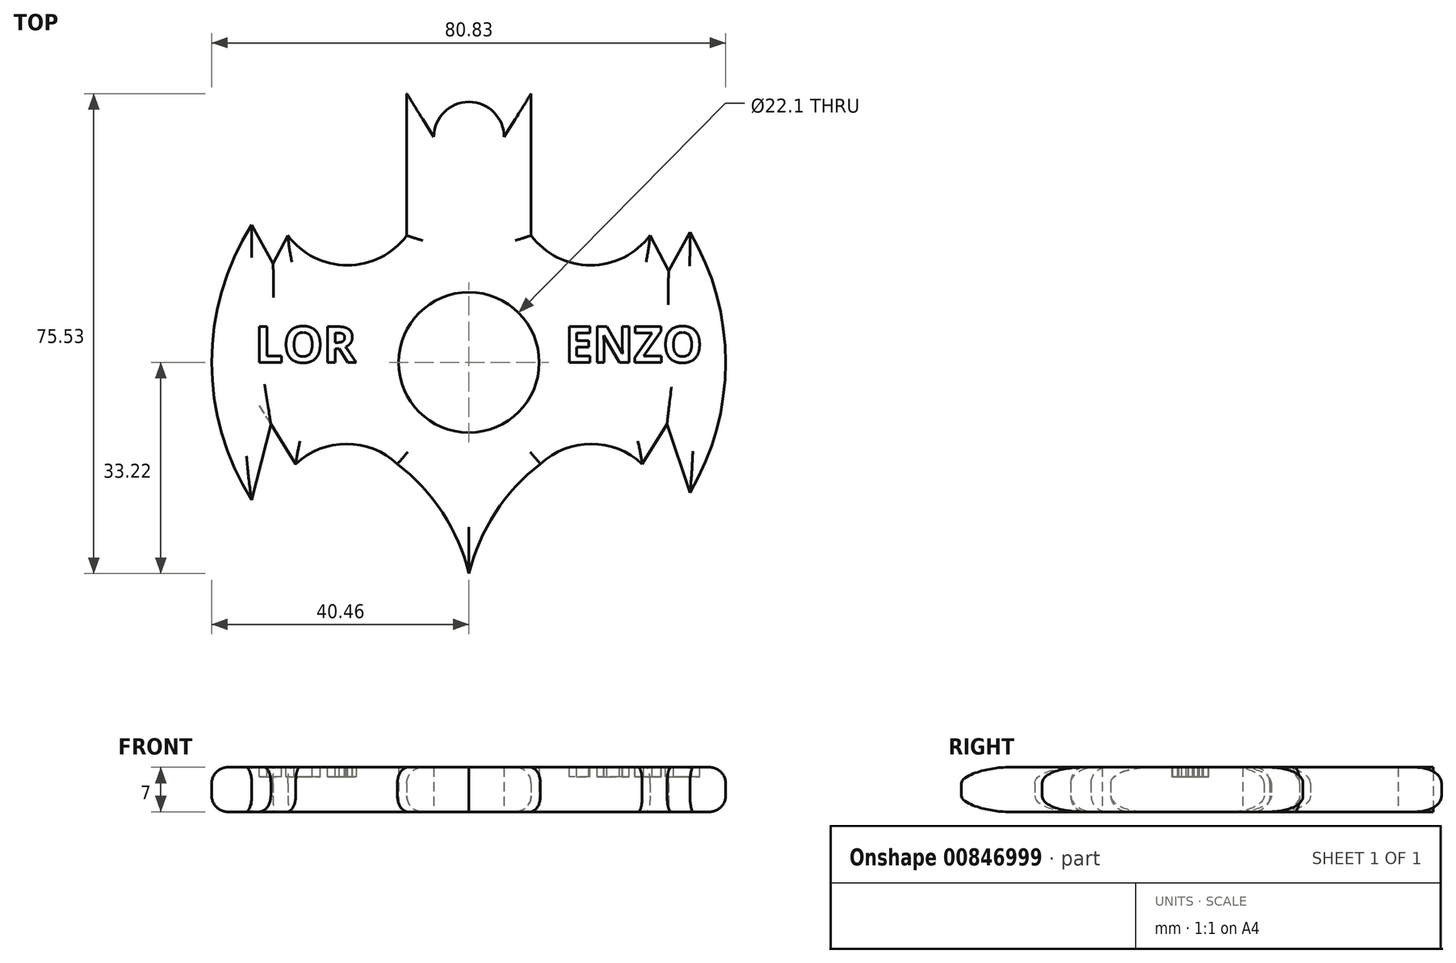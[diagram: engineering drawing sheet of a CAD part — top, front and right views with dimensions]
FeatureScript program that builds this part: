
annotation { "Feature Type Name" : "Feature", "Feature Type Description" : "" }
export const myFeature = defineFeature(function(context is Context, id is Id, definition is map)
    precondition{}
    {
        {
            var Q0;
            Q0=qCreatedBy(makeId("Top.planeOp"),FACE);
            var sketch = newSketch(context, id + "F0", { "sketchPlane" : qUnion([Q0])});
            skCircle(sketch, "E0", {"center": v(0, 0) * mm, "radius": 11.05 * mm});
            skLineSegment(sketch, "E1", {"start": v(-34.16, 56.83) * mm, "end": v(-34.16, -46.72) * mm, "construction": true});
            skArc(sketch, "E2", {"start": v(-34.16, 21.67) * mm, "mid": v(-40.46, 0) * mm, "end": v(-34.16, -21.67) * mm});
            skArc(sketch, "E3.MirrorCS", {"start": v(34.77, 20.51) * mm, "mid": v(40.37, 0) * mm, "end": v(34.77, -20.51) * mm});
            skLineSegment(sketch, "E4", {"start": v(-34.16, 21.67) * mm, "end": v(-30.8, 15.54) * mm});
            skLineSegment(sketch, "E5.MirrorCS", {"start": v(34.77, 20.51) * mm, "end": v(31.4, 14.38) * mm});
            skLineSegment(sketch, "E6", {"start": v(-30.8, 15.54) * mm, "end": v(-28.48, 19.97) * mm});
            skArc(sketch, "E7", {"start": v(-28.48, 19.97) * mm, "mid": v(-19.13, 15.3) * mm, "end": v(-9.78, 19.97) * mm});
            skArc(sketch, "E8.MirrorCS", {"start": v(-27.25, -16) * mm, "mid": v(-19.25, -12.83) * mm, "end": v(-11.25, -16) * mm});
            skArc(sketch, "E9.MirrorCS", {"start": v(27.25, -16) * mm, "mid": v(19.25, -12.83) * mm, "end": v(11.25, -16) * mm});
            skArc(sketch, "E10", {"start": v(0, -33.22) * mm, "mid": v(-4.15, -23.65) * mm, "end": v(-11.25, -16) * mm});
            skArc(sketch, "E11.MirrorCS", {"start": v(0, -33.22) * mm, "mid": v(4.15, -23.65) * mm, "end": v(11.25, -16) * mm});
            skLineSegment(sketch, "E12", {"start": v(-51.78, 0) * mm, "end": v(54.84, 0) * mm, "construction": true});
            skLineSegment(sketch, "E13", {"start": v(-34.16, -21.67) * mm, "end": v(-31.16, -9.72) * mm});
            skLineSegment(sketch, "E14", {"start": v(-31.16, -9.72) * mm, "end": v(-27.25, -16) * mm});
            skLineSegment(sketch, "E15.MirrorCS", {"start": v(34.77, -20.51) * mm, "end": v(31.16, -9.72) * mm});
            skLineSegment(sketch, "E16.MirrorCS", {"start": v(31.16, -9.72) * mm, "end": v(27.25, -16) * mm});
            skLineSegment(sketch, "E17", {"start": v(-9.78, 19.97) * mm, "end": v(-9.78, 42.3) * mm});
            skLineSegment(sketch, "E18", {"start": v(-9.78, 42.3) * mm, "end": v(-5.53, 35.46) * mm});
            skLineSegment(sketch, "E19", {"start": v(0, 73.5) * mm, "end": v(0, -54.17) * mm, "construction": true});
            skLineSegment(sketch, "E20.MirrorCS", {"start": v(9.78, 42.3) * mm, "end": v(5.53, 35.46) * mm});
            skArc(sketch, "E21", {"start": v(-5.53, 35.46) * mm, "mid": v(0, 41) * mm, "end": v(5.53, 35.46) * mm});
            skArc(sketch, "E22.MirrorCS", {"start": v(28.48, 19.97) * mm, "mid": v(19.13, 15.3) * mm, "end": v(9.78, 19.97) * mm});
            skLineSegment(sketch, "E23", {"start": v(9.78, 42.3) * mm, "end": v(9.78, 19.97) * mm});
            skLineSegment(sketch, "E24", {"start": v(28.48, 19.97) * mm, "end": v(31.4, 14.38) * mm});
            skSolve(sketch);
        }
        {
            var Q0;
            Q0=makeQuery(id+"F0.imprint","IMPRINT",FACE,{"disambiguationData":[TD([[makeQuery(id+"F0.imprint","IMPRINT",EDGE,{"derivedFrom":sQuery(id+"F0.wireOp",EDGE,"E0")}),-1.0]])]});
            extrude(context, id + "F1", {"entities" : qUnion([Q0]), "depth" : 7 * mm, "offsetDistance" : 25 * mm});
        }
        {
            var Q0;
            Q0=makeQuery(id+"F1.opExtrude","CAP_FACE",FACE,{"disambiguationData":[OSD([sQuery(id+"F0.wireOp",EDGE,"E0"),sQuery(id+"F0.wireOp",EDGE,"E2"),sQuery(id+"F0.wireOp",EDGE,"E3.MirrorCS"),sQuery(id+"F0.wireOp",EDGE,"E4"),sQuery(id+"F0.wireOp",EDGE,"E5.MirrorCS"),sQuery(id+"F0.wireOp",EDGE,"E6"),sQuery(id+"F0.wireOp",EDGE,"49427f80-c850-4576-a821-9a09c433f8150.MirrorCS"),sQuery(id+"F0.wireOp",EDGE,"E7"),sQuery(id+"F0.wireOp",EDGE,"E8.MirrorCS"),sQuery(id+"F0.wireOp",EDGE,"a26bc3be-dc20-46de-a755-517fbbfd5ccb0.MirrorCS"),sQuery(id+"F0.wireOp",EDGE,"E9.MirrorCS"),sQuery(id+"F0.wireOp",EDGE,"E10"),sQuery(id+"F0.wireOp",EDGE,"E11.MirrorCS"),sQuery(id+"F0.wireOp",EDGE,"E13"),sQuery(id+"F0.wireOp",EDGE,"E14"),sQuery(id+"F0.wireOp",EDGE,"E15.MirrorCS"),sQuery(id+"F0.wireOp",EDGE,"E16.MirrorCS"),sQuery(id+"F0.wireOp",EDGE,"E17"),sQuery(id+"F0.wireOp",EDGE,"E18"),sQuery(id+"F0.wireOp",EDGE,"136b1862-a08d-4cd8-944a-d1b0c07f457c0.MirrorCS"),sQuery(id+"F0.wireOp",EDGE,"E20.MirrorCS"),sQuery(id+"F0.wireOp",EDGE,"E21")])],"isStart":false});
            var sketch = newSketch(context, id + "F2", { "sketchPlane" : qUnion([Q0])});
            skText(sketch, "E25", { "text": "LOR                ENZO", "fontName": "OpenSans-Bold.ttf"});
            const initialGuessF2  = {"E25": [-0.03368, 0, 1, 0, 0.00568]};
            skSetInitialGuess(sketch, initialGuessF2);
            skSolve(sketch);
        }
        {
            var Q0;
            Q0 = qSketchRegion(id + "F2", true);
            extrude(context, id + "F3", {"entities" : qUnion([Q0]), "operationType" : NewBodyOperationType.REMOVE, "oppositeDirection" : true, "depth" : 1.5 * mm, "offsetDistance" : 25 * mm});
        }
        {
            var Q0;
            Q0=makeQuery(id+"F1.opExtrude","CAP_EDGE",EDGE,{"disambiguationData":[OSD([sQuery(id+"F0.wireOp",EDGE,"E2")])],"isStart":false});
            var Q1;
            Q1=makeQuery(id+"F1.opExtrude","CAP_EDGE",EDGE,{"disambiguationData":[OSD([sQuery(id+"F0.wireOp",EDGE,"E4")])],"isStart":false});
            var Q2;
            Q2=makeQuery(id+"F1.opExtrude","CAP_EDGE",EDGE,{"disambiguationData":[OSD([sQuery(id+"F0.wireOp",EDGE,"E6")])],"isStart":false});
            var Q3;
            Q3=makeQuery(id+"F1.opExtrude","CAP_EDGE",EDGE,{"disambiguationData":[OSD([sQuery(id+"F0.wireOp",EDGE,"E7")])],"isStart":false});
            var Q4;
            Q4=makeQuery(id+"F1.opExtrude","CAP_EDGE",EDGE,{"disambiguationData":[OSD([sQuery(id+"F0.wireOp",EDGE,"E17")])],"isStart":false});
            var Q5;
            Q5=makeQuery(id+"F1.opExtrude","CAP_EDGE",EDGE,{"disambiguationData":[OSD([sQuery(id+"F0.wireOp",EDGE,"E23")])],"isStart":false});
            var Q6;
            Q6=makeQuery(id+"F1.opExtrude","CAP_EDGE",EDGE,{"disambiguationData":[OSD([sQuery(id+"F0.wireOp",EDGE,"E22.MirrorCS")])],"isStart":false});
            var Q7;
            Q7=makeQuery(id+"F1.opExtrude","CAP_EDGE",EDGE,{"disambiguationData":[OSD([sQuery(id+"F0.wireOp",EDGE,"E24")])],"isStart":false});
            var Q8;
            Q8=makeQuery(id+"F1.opExtrude","CAP_EDGE",EDGE,{"disambiguationData":[OSD([sQuery(id+"F0.wireOp",EDGE,"E5.MirrorCS")])],"isStart":false});
            var Q9;
            Q9=makeQuery(id+"F1.opExtrude","CAP_EDGE",EDGE,{"disambiguationData":[OSD([sQuery(id+"F0.wireOp",EDGE,"E3.MirrorCS")])],"isStart":false});
            var Q10;
            Q10=makeQuery(id+"F1.opExtrude","CAP_EDGE",EDGE,{"disambiguationData":[OSD([sQuery(id+"F0.wireOp",EDGE,"E15.MirrorCS")])],"isStart":false});
            var Q11;
            Q11=makeQuery(id+"F1.opExtrude","CAP_EDGE",EDGE,{"disambiguationData":[OSD([sQuery(id+"F0.wireOp",EDGE,"E16.MirrorCS")])],"isStart":false});
            var Q12;
            Q12=makeQuery(id+"F1.opExtrude","CAP_EDGE",EDGE,{"disambiguationData":[OSD([sQuery(id+"F0.wireOp",EDGE,"E9.MirrorCS")])],"isStart":false});
            var Q13;
            Q13=makeQuery(id+"F1.opExtrude","CAP_EDGE",EDGE,{"disambiguationData":[OSD([sQuery(id+"F0.wireOp",EDGE,"E11.MirrorCS")])],"isStart":false});
            var Q14;
            Q14=makeQuery(id+"F1.opExtrude","CAP_EDGE",EDGE,{"disambiguationData":[OSD([sQuery(id+"F0.wireOp",EDGE,"E10")])],"isStart":false});
            var Q15;
            Q15=makeQuery(id+"F1.opExtrude","CAP_EDGE",EDGE,{"disambiguationData":[OSD([sQuery(id+"F0.wireOp",EDGE,"E8.MirrorCS")])],"isStart":false});
            var Q16;
            Q16=makeQuery(id+"F1.opExtrude","CAP_EDGE",EDGE,{"disambiguationData":[OSD([sQuery(id+"F0.wireOp",EDGE,"E14")])],"isStart":false});
            var Q17;
            Q17=makeQuery(id+"F1.opExtrude","CAP_EDGE",EDGE,{"disambiguationData":[OSD([sQuery(id+"F0.wireOp",EDGE,"E13")])],"isStart":false});
            fillet(context, id + "F4", {"entities" : qUnion([Q0, Q1, Q2, Q3, Q4, Q5, Q6, Q7, Q8, Q9, Q10, Q11, Q12, Q13, Q14, Q15, Q16, Q17]), "radius" : 2.5 * mm, "tangentPropagation" : true, "allowEdgeOverflow" : false});
        }
        {
            var Q0;
            Q0=makeQuery(id+"F1.opExtrude","CAP_EDGE",EDGE,{"disambiguationData":[OSD([sQuery(id+"F0.wireOp",EDGE,"E2")])],"isStart":true});
            var Q1;
            Q1=makeQuery(id+"F1.opExtrude","CAP_EDGE",EDGE,{"disambiguationData":[OSD([sQuery(id+"F0.wireOp",EDGE,"E4")])],"isStart":true});
            var Q2;
            Q2=makeQuery(id+"F1.opExtrude","CAP_EDGE",EDGE,{"disambiguationData":[OSD([sQuery(id+"F0.wireOp",EDGE,"E6")])],"isStart":true});
            var Q3;
            Q3=makeQuery(id+"F1.opExtrude","CAP_EDGE",EDGE,{"disambiguationData":[OSD([sQuery(id+"F0.wireOp",EDGE,"E7")])],"isStart":true});
            var Q4;
            Q4=makeQuery(id+"F1.opExtrude","CAP_EDGE",EDGE,{"disambiguationData":[OSD([sQuery(id+"F0.wireOp",EDGE,"E17")])],"isStart":true});
            var Q5;
            Q5=makeQuery(id+"F1.opExtrude","CAP_EDGE",EDGE,{"disambiguationData":[OSD([sQuery(id+"F0.wireOp",EDGE,"E22.MirrorCS")])],"isStart":true});
            var Q6;
            Q6=makeQuery(id+"F1.opExtrude","CAP_EDGE",EDGE,{"disambiguationData":[OSD([sQuery(id+"F0.wireOp",EDGE,"E24")])],"isStart":true});
            var Q7;
            Q7=makeQuery(id+"F1.opExtrude","CAP_EDGE",EDGE,{"disambiguationData":[OSD([sQuery(id+"F0.wireOp",EDGE,"E5.MirrorCS")])],"isStart":true});
            var Q8;
            {var subQ0=sQuery(id+"F0.wireOp",EDGE,"E3.MirrorCS");Q8=makeQuery(id+"F4.opFillet","BLEND_EDGE",EDGE,{"blendedFrom":[makeQuery(id+"F1.opExtrude","CAP_EDGE",EDGE,{"disambiguationData":[OSD([subQ0])],"isStart":false}),makeQuery(id+"F1.opExtrude","SWEPT_FACE",FACE,{"disambiguationData":[OSD([subQ0])]})],"blendedInto":[makeQuery(id+"F1.opExtrude","SWEPT_FACE",FACE,{"disambiguationData":[OSD([subQ0])]})]});}
            var Q9;
            Q9=makeQuery(id+"F1.opExtrude","CAP_EDGE",EDGE,{"disambiguationData":[OSD([sQuery(id+"F0.wireOp",EDGE,"E15.MirrorCS")])],"isStart":true});
            var Q10;
            Q10=makeQuery(id+"F1.opExtrude","CAP_EDGE",EDGE,{"disambiguationData":[OSD([sQuery(id+"F0.wireOp",EDGE,"E16.MirrorCS")])],"isStart":true});
            var Q11;
            Q11=makeQuery(id+"F1.opExtrude","CAP_EDGE",EDGE,{"disambiguationData":[OSD([sQuery(id+"F0.wireOp",EDGE,"E9.MirrorCS")])],"isStart":true});
            var Q12;
            Q12=makeQuery(id+"F1.opExtrude","CAP_EDGE",EDGE,{"disambiguationData":[OSD([sQuery(id+"F0.wireOp",EDGE,"E11.MirrorCS")])],"isStart":true});
            var Q13;
            {var subQ0=sQuery(id+"F0.wireOp",EDGE,"E10");Q13=makeQuery(id+"F4.opFillet","BLEND_EDGE",EDGE,{"blendedFrom":[makeQuery(id+"F1.opExtrude","CAP_EDGE",EDGE,{"disambiguationData":[OSD([subQ0])],"isStart":false}),makeQuery(id+"F1.opExtrude","SWEPT_FACE",FACE,{"disambiguationData":[OSD([subQ0])]})],"blendedInto":[makeQuery(id+"F1.opExtrude","SWEPT_FACE",FACE,{"disambiguationData":[OSD([subQ0])]})]});}
            var Q14;
            Q14=makeQuery(id+"F1.opExtrude","CAP_EDGE",EDGE,{"disambiguationData":[OSD([sQuery(id+"F0.wireOp",EDGE,"E8.MirrorCS")])],"isStart":true});
            var Q15;
            {var subQ0=sQuery(id+"F0.wireOp",EDGE,"E14");Q15=makeQuery(id+"F4.opFillet","BLEND_EDGE",EDGE,{"blendedFrom":[makeQuery(id+"F1.opExtrude","CAP_EDGE",EDGE,{"disambiguationData":[OSD([subQ0])],"isStart":false}),makeQuery(id+"F1.opExtrude","SWEPT_FACE",FACE,{"disambiguationData":[OSD([subQ0])]})],"blendedInto":[makeQuery(id+"F1.opExtrude","SWEPT_FACE",FACE,{"disambiguationData":[OSD([subQ0])]})]});}
            var Q16;
            Q16=makeQuery(id+"F1.opExtrude","CAP_EDGE",EDGE,{"disambiguationData":[OSD([sQuery(id+"F0.wireOp",EDGE,"E10")])],"isStart":true});
            var Q17;
            Q17=makeQuery(id+"F1.opExtrude","CAP_EDGE",EDGE,{"disambiguationData":[OSD([sQuery(id+"F0.wireOp",EDGE,"E13")])],"isStart":true});
            var Q18;
            Q18=makeQuery(id+"F1.opExtrude","CAP_EDGE",EDGE,{"disambiguationData":[OSD([sQuery(id+"F0.wireOp",EDGE,"E23")])],"isStart":true});
            var Q19;
            Q19=makeQuery(id+"F1.opExtrude","CAP_EDGE",EDGE,{"disambiguationData":[OSD([sQuery(id+"F0.wireOp",EDGE,"E3.MirrorCS")])],"isStart":true});
            fillet(context, id + "F5", {"entities" : qUnion([Q0, Q1, Q2, Q3, Q4, Q5, Q6, Q7, Q8, Q9, Q10, Q11, Q12, Q13, Q14, Q15, Q16, Q17, Q18, Q19]), "radius" : 2.5 * mm, "tangentPropagation" : true, "allowEdgeOverflow" : false});
        }
    });
